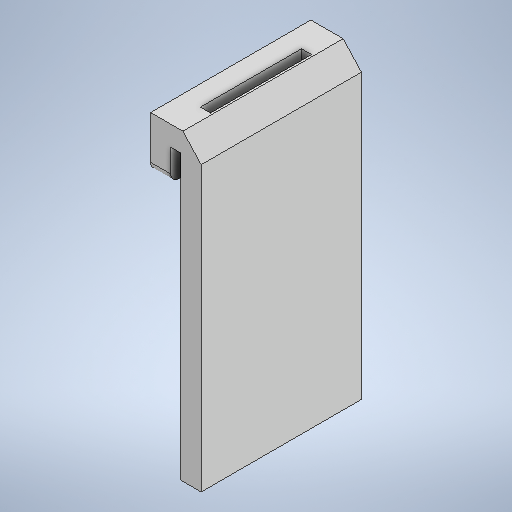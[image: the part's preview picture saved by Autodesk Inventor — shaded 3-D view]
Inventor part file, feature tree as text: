
AUTODESK INVENTOR PART (.ipt)
format: ipt  version: 2025 (Build 290162000, 162)  size: 259,584 bytes
history: native  units: mm
features: extrude x3, sketch x3, fillet x1
ambient origin geometry x8: Origin, YZ Plane, XZ Plane, XY Plane, X Axis, Y Axis, Z Axis, Center Point
bodies: Solid1 (feature_tree)
feature tree (7):
  extrude  "Extrusion1"  Depth=25.4mm
  extrude  "Extrusion2"  Depth=76.2mm TaperAngle=0.0deg
  extrude  "Extrusion3"  Depth=2.0mm
  fillet  "Fillet1"  Radius=5.0mm
  sketch  "Sketch1"  dims[d0=2.54mm d1=25.4mm]
  sketch  "Sketch2"  dims[d2=12.7mm d3=76.2mm d4=0.0mm]
  sketch  "Sketch3"  dims[d5=5.0mm d6=0.5mm d7=5.0mm d8=0.0mm d9=0.0mm d10=12.7mm d11=25.4mm d13=19.05mm d14=10.0mm d15=0.0mm d16=2.0mm]
